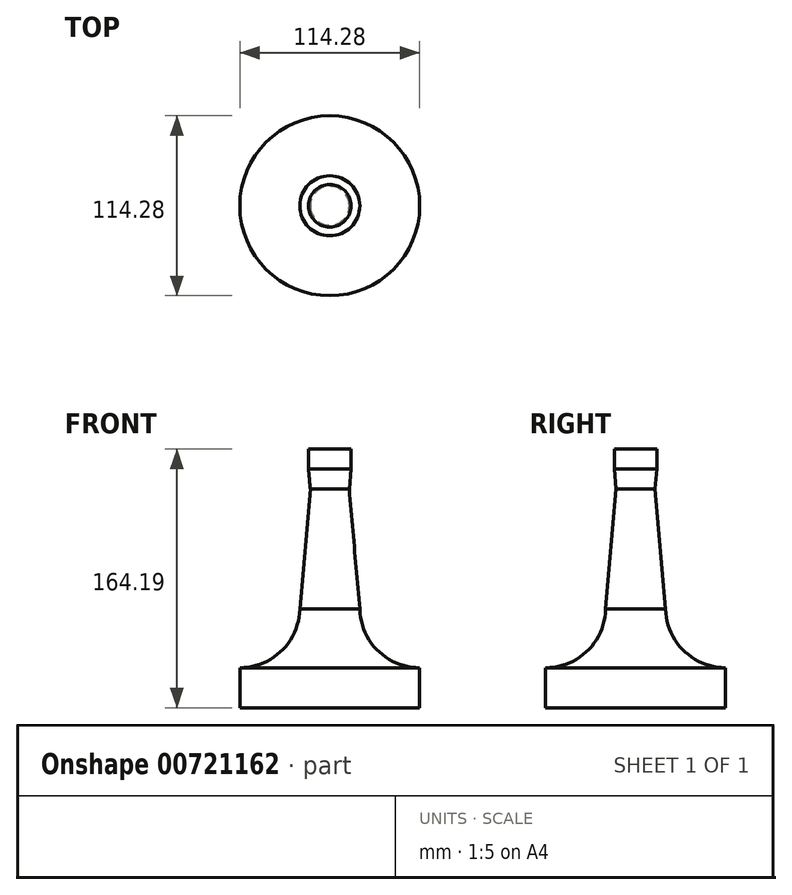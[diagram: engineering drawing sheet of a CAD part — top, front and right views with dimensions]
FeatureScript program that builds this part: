
annotation { "Feature Type Name" : "Feature", "Feature Type Description" : "" }
export const myFeature = defineFeature(function(context is Context, id is Id, definition is map)
    precondition{}
    {
        {
            var Q0;
            Q0=qCreatedBy(makeId("Front.planeOp"),FACE);
            var sketch = newSketch(context, id + "F0", { "sketchPlane" : qUnion([Q0])});
            skLineSegment(sketch, "E0", {"start": v(0, 0) * mm, "end": v(-57.14, 0) * mm});
            skLineSegment(sketch, "E1", {"start": v(-57.14, 0) * mm, "end": v(-57.14, 25.4) * mm});
            skArc(sketch, "E2", {"start": v(-57.14, 25.4) * mm, "mid": v(-30.52, 36.24) * mm, "end": v(-19.05, 62.6) * mm});
            skLineSegment(sketch, "E3", {"start": v(-19.05, 62.6) * mm, "end": v(0, 62.6) * mm});
            skLineSegment(sketch, "E4", {"start": v(0, 62.6) * mm, "end": v(0, 0) * mm});
            skSolve(sketch);
        }
        {
            var Q0;
            Q0 = qSketchRegion(id + "F0", true);
            var Q1;
            Q1=sQuery(id+"F0.wireOp",EDGE,"E4");
            revolve(context, id + "F1", {"surfaceOperationType" : NewSurfaceOperationType.NEW, "entities" : qUnion([Q0]), "axis" : qUnion([Q1]), "revolveType" : RevolveType.FULL});
        }
        {
            var Q0;
            Q0=makeQuery(id+"F1.opRevolve","SWEPT_FACE",FACE,{"disambiguationData":[OSD([sQuery(id+"F0.wireOp",EDGE,"E3")])]});
            extrude(context, id + "F2", {"entities" : qUnion([Q0]), "operationType" : NewBodyOperationType.ADD, "depth" : 76.2 * mm, "offsetDistance" : 25.4 * mm, "hasDraft" : true, "draftAngle" : 5 * degree, "draftPullDirection" : true});
        }
        {
            var Q0;
            Q0=makeQuery(id+"F2.opExtrude","CAP_FACE",FACE,{"disambiguationData":[OSD([sQuery(id+"F0.wireOp",EDGE,"E3")])],"isStart":false});
            extrude(context, id + "F3", {"entities" : qUnion([Q0]), "operationType" : NewBodyOperationType.ADD, "depth" : 12.7 * mm, "offsetDistance" : 25.4 * mm, "hasDraft" : true, "draftAngle" : 5 * degree});
        }
        {
            var Q0;
            Q0=makeQuery(id+"F3.opExtrude","CAP_FACE",FACE,{"disambiguationData":[OSD([sQuery(id+"F0.wireOp",EDGE,"E3")])],"isStart":false});
            extrude(context, id + "F4", {"entities" : qUnion([Q0]), "operationType" : NewBodyOperationType.ADD, "depth" : 12.7 * mm, "offsetDistance" : 25.4 * mm});
        }
    });
